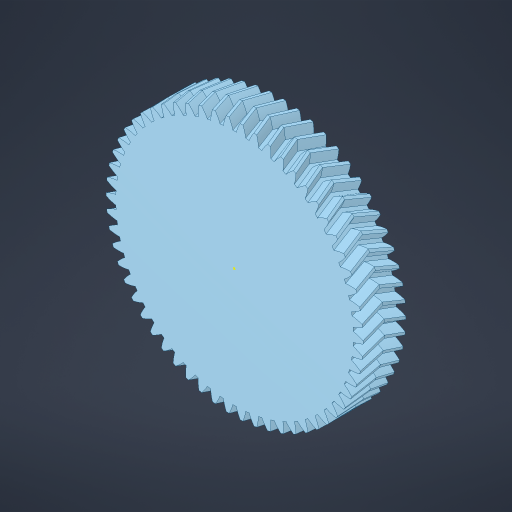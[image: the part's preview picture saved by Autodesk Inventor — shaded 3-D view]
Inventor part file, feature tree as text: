
AUTODESK INVENTOR PART (.ipt)
format: ipt  version: 2023.4 (Build 274418000, 418)  size: 1,323,520 bytes
history: native  units: in
note: dims shown in document units (in); Inventor stores cm internally (conversion verified against a paired STEP export)
features: sketch x1, other x1
ambient origin geometry x8: Origin, YZ Plane, XZ Plane, XY Plane, X Axis, Y Axis, Z Axis, Center Point
bodies: Solid1 (feature_tree)
feature tree (2):
  sketch  "Sketch1"
  other  "Helical 2M 58T"
